# Revit family: VR3IF-4103-LRC
name_source: partatom
category: Lighting Fixtures
units: mm (PartAtom-declared; Revit-internal decimal feet)

## family parameters
Always vertical = Yes
Cut with Voids When Loaded = No
Host = Ceiling
Light Source = Yes
OmniClass Number = 23.80.70.11.14.17
OmniClass Title = Direct/Indirect
Part Type = Normal
Room Calculation Point = No
Round Connector Dimension = Use Diameter
Shared = No

## types (4) — shared parameters
Assembly Code = D5020200
Color Filter = 16777215
Description = LED Behavioal Health Anti-Ligature
Dimming Lamp Color Temperature Shift = <None>
DoorFrame = Polycarbonate - Viscor - Clear Lens  0.375" Thick
Emit Shape Visible in Rendering = No
Emit from Rectangle Length = 4' - 3 1/16"
Emit from Rectangle Width = 2' - 3 7/8"
Exam Lens = Polycarbonate - Viscor - Frosted Flat
Housing Finish = Metal - Viscor - White
Lamp = LED
Length = 4' - 3 1/16"
Lens ambient = Acrylic - Viscor - Frosted Round
Manufacturer = CERTOLUX by VISCOR
Model = VR3IF-4103-LRC
Tilt Angle = 90.00°
URL = https://www.viscor.com
Voltage = 120 V
Width = 2' - 3 7/8"

## per-type parameters (varying)
| type | Apparent Load | Lamp Wattage | Photometric Web File |
| VR3IF-4103-LED835K20L_34L-835K100L-P47 (ALL ON) | 160 VA | 160 VA | VR3IF-4103-LED835K20L_34L-835K100L-P47 (ALL ON).IES |
| VR3IF-4103-LED835K20L_34L-835K100L-P47 (AMBIENT ON ONLY) | 35 VA | 35 VA | VR3IF-4103-LED835K20L_34L-835K100L-P47 (AMBIENT ON ONLY).IES |
| VR3IF-4103-LED835K20L_34L-835K100L-P47 (EXAM ON ONLY) | 101 VA | 101 VA | VR3IF-4103-LED835K20L_34L-835K100L-P47 (EXAM ON ONLY).IES |
| VR3IF-4103-LED835K20L_34L-835K100L-P47 (READING ON ONLY) | 23 VA | 23 VA | VR3IF-4103-LED835K20L_34L-835K100L-P47 (READING ON ONLY).IES |

## geometry (parser evidence)
native form markers: Sweep x2
no freeform markers — native parametric forms only
